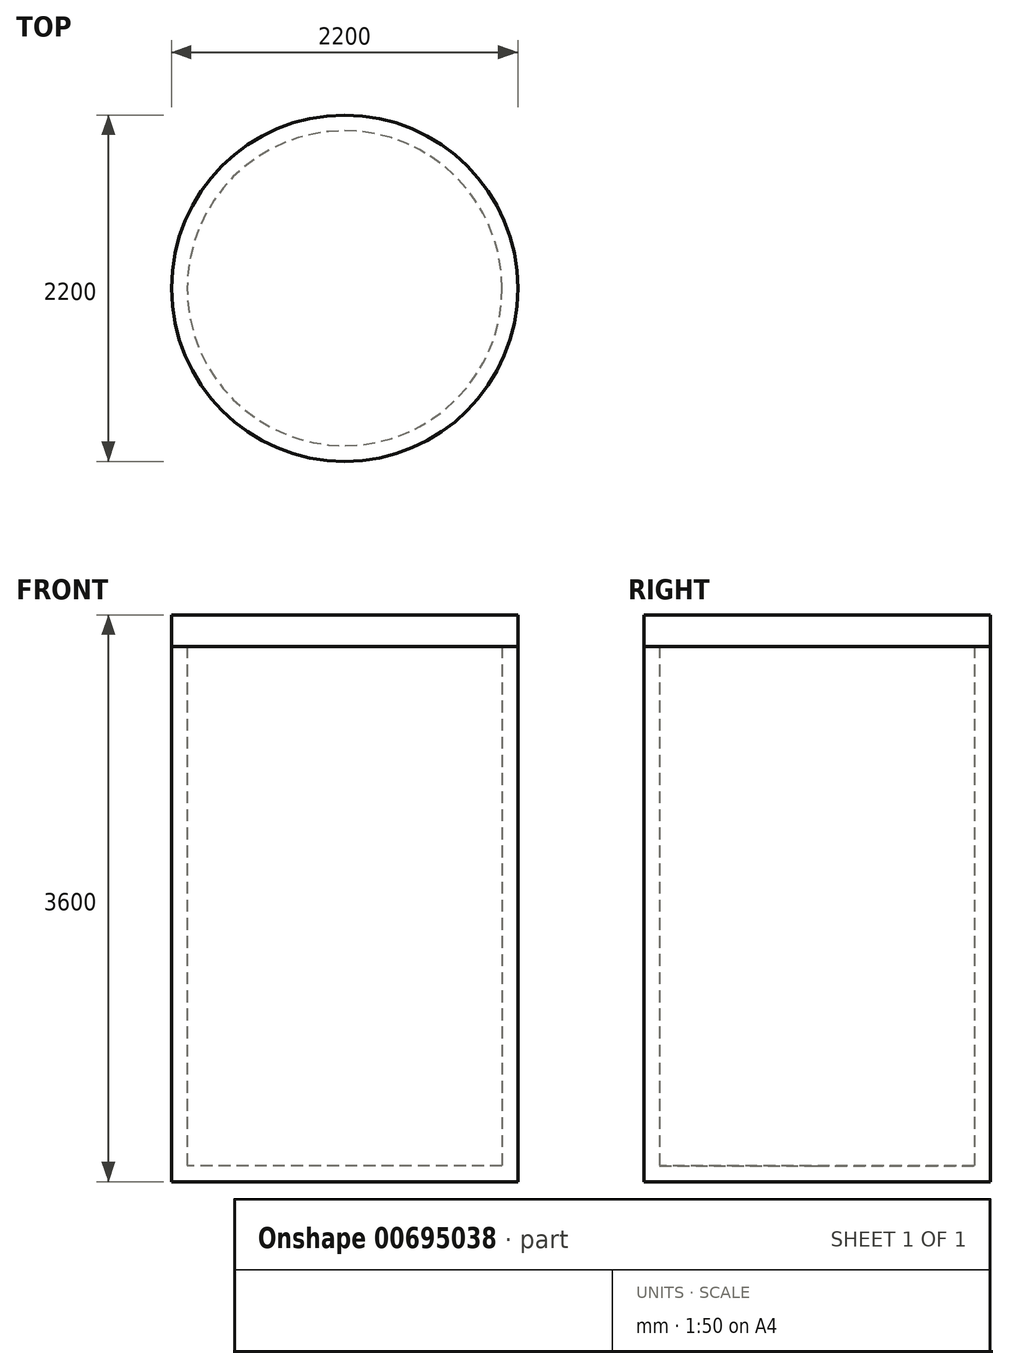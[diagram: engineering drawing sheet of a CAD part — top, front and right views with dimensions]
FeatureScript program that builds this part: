
annotation { "Feature Type Name" : "Feature", "Feature Type Description" : "" }
export const myFeature = defineFeature(function(context is Context, id is Id, definition is map)
    precondition{}
    {
        {
            var Q0;
            Q0=qCreatedBy(makeId("Top.planeOp"),FACE);
            var sketch = newSketch(context, id + "F0", { "sketchPlane" : qUnion([Q0])});
            skCircle(sketch, "E0", {"center": v(0, 0) * mm, "radius": 1100 * mm});
            skSolve(sketch);
        }
        {
            var Q0;
            Q0=makeQuery(id+"F0.imprint","IMPRINT",FACE,{"disambiguationData":[TD([[makeQuery(id+"F0.imprint","IMPRINT",EDGE,{"derivedFrom":sQuery(id+"F0.wireOp",EDGE,"E0")}),1.0]])]});
            extrude(context, id + "F1", {"entities" : qUnion([Q0]), "depth" : 3400 * mm, "offsetDistance" : 25 * mm});
        }
        {
            var Q0;
            Q0=makeQuery(id+"F1.opExtrude","CAP_FACE",FACE,{"disambiguationData":[OSD([sQuery(id+"F0.wireOp",EDGE,"E0")])],"isStart":false});
            shell(context, id + "F2", {"entities" : qUnion([Q0]), "thickness" : 100 * mm});
        }
        {
            var Q0;
            Q0=makeQuery(id+"F1.opExtrude","CAP_FACE",FACE,{"disambiguationData":[OSD([sQuery(id+"F0.wireOp",EDGE,"E0")])],"isStart":false});
            var sketch = newSketch(context, id + "F3", { "sketchPlane" : qUnion([Q0])});
            skCircle(sketch, "E1", {"center": v(0, 0) * mm, "radius": 1100 * mm});
            skSolve(sketch);
        }
        {
            var Q0;
            Q0 = qSketchRegion(id + "F3", true);
            extrude(context, id + "F4", {"entities" : qUnion([Q0]), "depth" : 200 * mm, "offsetDistance" : 25 * mm});
        }
    });
